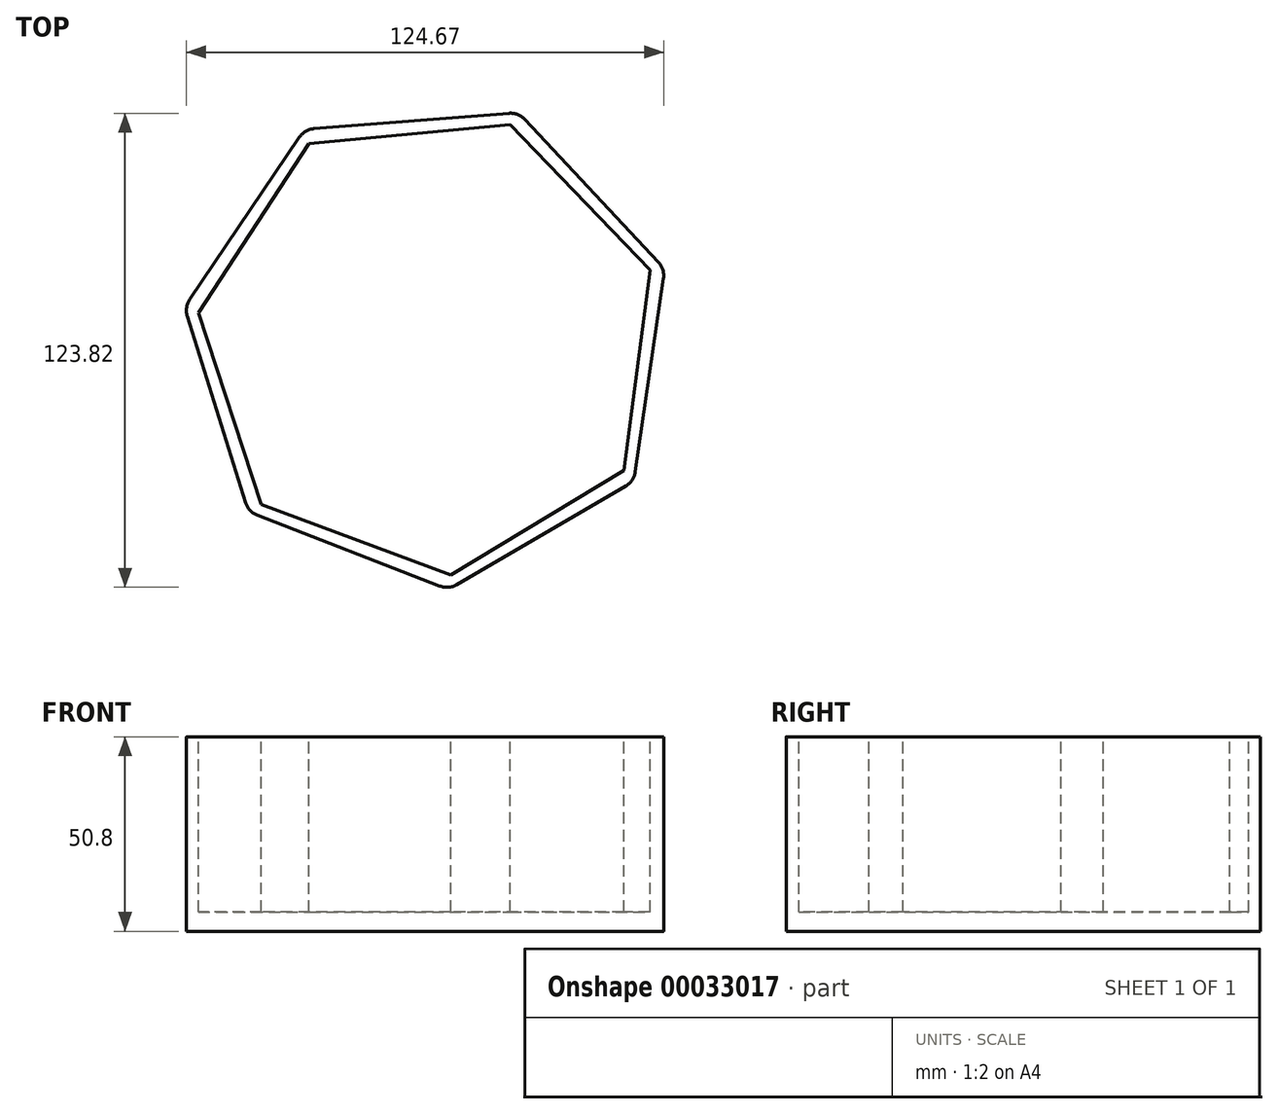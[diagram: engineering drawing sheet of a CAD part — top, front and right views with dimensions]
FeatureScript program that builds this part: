
annotation { "Feature Type Name" : "Feature", "Feature Type Description" : "" }
export const myFeature = defineFeature(function(context is Context, id is Id, definition is map)
    precondition{}
    {
        {
            var Q0;
            Q0=qCreatedBy(makeId("Top.planeOp"),FACE);
            var sketch = newSketch(context, id + "F0", { "sketchPlane" : qUnion([Q0])});
            skCircle(sketch, "E0.cCircle", {"center": v(0, 0) * mm, "radius": 64.55 * mm, "construction": true});
            skLineSegment(sketch, "E0.0", {"start": v(-32.52, 55.76) * mm, "end": v(23.32, 60.2) * mm});
            skLineSegment(sketch, "E0.1", {"start": v(23.32, 60.2) * mm, "end": v(61.6, 19.3) * mm});
            skLineSegment(sketch, "E0.2", {"start": v(61.6, 19.3) * mm, "end": v(53.5, -36.13) * mm});
            skLineSegment(sketch, "E0.3", {"start": v(53.5, -36.13) * mm, "end": v(5.1, -64.35) * mm});
            skLineSegment(sketch, "E0.4", {"start": v(5.1, -64.35) * mm, "end": v(-47.13, -44.11) * mm});
            skLineSegment(sketch, "E0.5", {"start": v(-47.13, -44.11) * mm, "end": v(-63.87, 9.35) * mm});
            skLineSegment(sketch, "E0.6", {"start": v(-63.87, 9.35) * mm, "end": v(-32.52, 55.76) * mm});
            skSolve(sketch);
        }
        {
            var Q0;
            Q0=makeQuery(id+"F0.imprint","IMPRINT",FACE,{"disambiguationData":[TD([[makeQuery(id+"F0.imprint","IMPRINT",EDGE,{"derivedFrom":sQuery(id+"F0.wireOp",EDGE,"E0.0")}),-1.0]])]});
            extrude(context, id + "F1", {"entities" : qUnion([Q0]), "depth" : 50.8 * mm});
        }
        {
            var Q0;
            Q0=makeQuery(id+"F1.opExtrude","CAP_FACE",FACE,{"disambiguationData":[OSD([sQuery(id+"F0.wireOp",EDGE,"E0.0"),sQuery(id+"F0.wireOp",EDGE,"E0.1"),sQuery(id+"F0.wireOp",EDGE,"E0.2"),sQuery(id+"F0.wireOp",EDGE,"E0.3"),sQuery(id+"F0.wireOp",EDGE,"E0.4"),sQuery(id+"F0.wireOp",EDGE,"E0.5"),sQuery(id+"F0.wireOp",EDGE,"E0.6")])],"isStart":false});
            var sketch = newSketch(context, id + "F2", { "sketchPlane" : qUnion([Q0])});
            skCircle(sketch, "E1.cCircle", {"center": v(0, 0) * mm, "radius": 60.78 * mm, "construction": true});
            skLineSegment(sketch, "E1.0", {"start": v(-31.38, 52.06) * mm, "end": v(21.14, 56.99) * mm});
            skLineSegment(sketch, "E1.1", {"start": v(21.14, 56.99) * mm, "end": v(57.73, 19) * mm});
            skLineSegment(sketch, "E1.2", {"start": v(57.73, 19) * mm, "end": v(50.86, -33.29) * mm});
            skLineSegment(sketch, "E1.3", {"start": v(50.86, -33.29) * mm, "end": v(5.68, -60.51) * mm});
            skLineSegment(sketch, "E1.4", {"start": v(5.68, -60.51) * mm, "end": v(-43.77, -42.17) * mm});
            skLineSegment(sketch, "E1.5", {"start": v(-43.77, -42.17) * mm, "end": v(-60.26, 7.93) * mm});
            skLineSegment(sketch, "E1.6", {"start": v(-60.26, 7.93) * mm, "end": v(-31.38, 52.06) * mm});
            skSolve(sketch);
        }
        {
            var Q0;
            Q0=makeQuery(id+"F2.imprint","IMPRINT",FACE,{"disambiguationData":[TD([[makeQuery(id+"F2.imprint","IMPRINT",EDGE,{"derivedFrom":sQuery(id+"F2.wireOp",EDGE,"E1.0")}),-1.0]])]});
            extrude(context, id + "F3", {"entities" : qUnion([Q0]), "operationType" : NewBodyOperationType.REMOVE, "oppositeDirection" : true, "depth" : 45.72 * mm});
        }
        {
            var Q0;
            Q0=makeQuery(id+"F1.opExtrude","SWEPT_EDGE",EDGE,{"disambiguationData":[OSD([sQuery(id+"F0.wireOp",EDGE,"E0.5"),sQuery(id+"F0.wireOp",EDGE,"E0.6")])]});
            var Q1;
            Q1=makeQuery(id+"F1.opExtrude","SWEPT_EDGE",EDGE,{"disambiguationData":[OSD([sQuery(id+"F0.wireOp",EDGE,"E0.0"),sQuery(id+"F0.wireOp",EDGE,"E0.6")])]});
            var Q2;
            Q2=makeQuery(id+"F1.opExtrude","SWEPT_EDGE",EDGE,{"disambiguationData":[OSD([sQuery(id+"F0.wireOp",EDGE,"E0.0"),sQuery(id+"F0.wireOp",EDGE,"E0.1")])]});
            var Q3;
            Q3=makeQuery(id+"F1.opExtrude","SWEPT_EDGE",EDGE,{"disambiguationData":[OSD([sQuery(id+"F0.wireOp",EDGE,"E0.1"),sQuery(id+"F0.wireOp",EDGE,"E0.2")])]});
            var Q4;
            Q4=makeQuery(id+"F1.opExtrude","SWEPT_EDGE",EDGE,{"disambiguationData":[OSD([sQuery(id+"F0.wireOp",EDGE,"E0.2"),sQuery(id+"F0.wireOp",EDGE,"E0.3")])]});
            var Q5;
            Q5=makeQuery(id+"F1.opExtrude","SWEPT_EDGE",EDGE,{"disambiguationData":[OSD([sQuery(id+"F0.wireOp",EDGE,"E0.4"),sQuery(id+"F0.wireOp",EDGE,"E0.5")])]});
            var Q6;
            Q6=makeQuery(id+"F1.opExtrude","SWEPT_EDGE",EDGE,{"disambiguationData":[OSD([sQuery(id+"F0.wireOp",EDGE,"E0.3"),sQuery(id+"F0.wireOp",EDGE,"E0.4")])]});
            fillet(context, id + "F4", {"entities" : qUnion([Q0, Q1, Q2, Q3, Q4, Q5, Q6]), "radius" : 5.08 * mm, "tangentPropagation" : true, "allowEdgeOverflow" : false});
        }
    });
